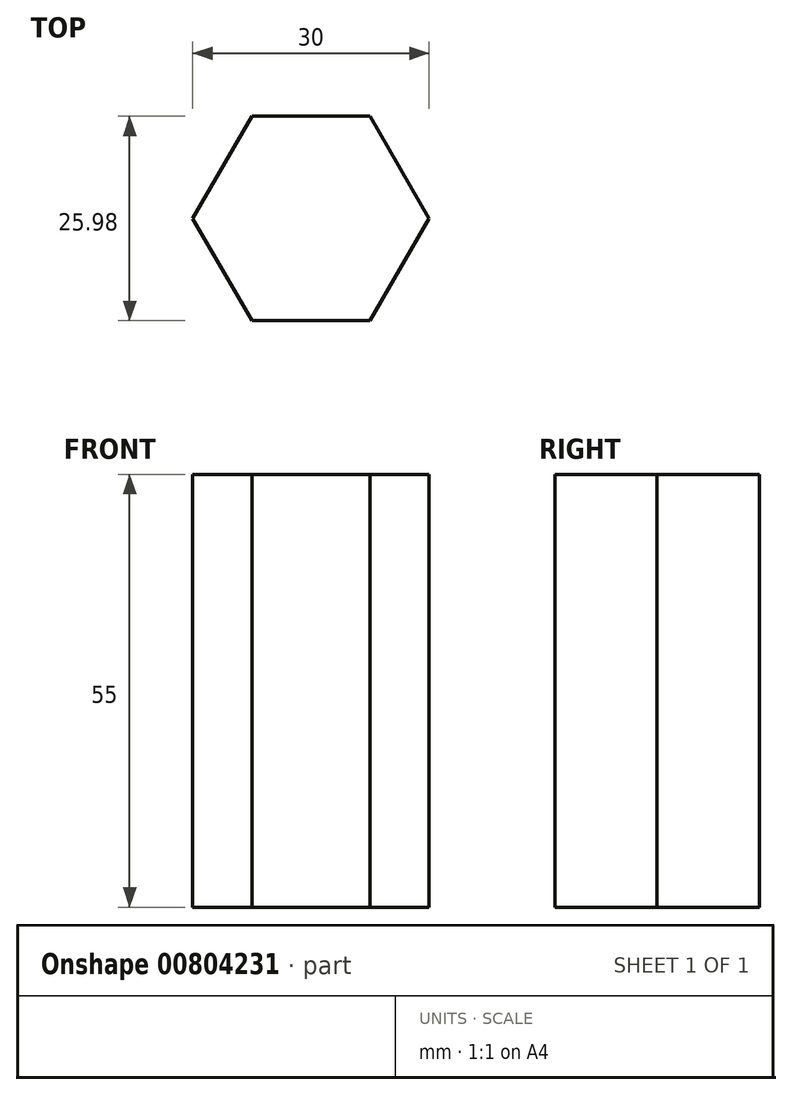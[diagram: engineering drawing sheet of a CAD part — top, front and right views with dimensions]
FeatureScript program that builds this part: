
annotation { "Feature Type Name" : "Feature", "Feature Type Description" : "" }
export const myFeature = defineFeature(function(context is Context, id is Id, definition is map)
    precondition{}
    {
        {
            var Q0;
            Q0=qCreatedBy(makeId("Top.planeOp"),FACE);
            var sketch = newSketch(context, id + "F0", { "sketchPlane" : qUnion([Q0])});
            skCircle(sketch, "E0.cCircle", {"center": v(0, 0) * mm, "radius": 15 * mm, "construction": true});
            skLineSegment(sketch, "E0.0", {"start": v(15, 0) * mm, "end": v(7.5, -13) * mm});
            skLineSegment(sketch, "E0.1", {"start": v(7.5, -13) * mm, "end": v(-7.5, -13) * mm});
            skLineSegment(sketch, "E0.2", {"start": v(-7.5, -13) * mm, "end": v(-15, 0) * mm});
            skLineSegment(sketch, "E0.3", {"start": v(-15, 0) * mm, "end": v(-7.5, 13) * mm});
            skLineSegment(sketch, "E0.4", {"start": v(-7.5, 13) * mm, "end": v(7.5, 13) * mm});
            skLineSegment(sketch, "E0.5", {"start": v(7.5, 13) * mm, "end": v(15, 0) * mm});
            skSolve(sketch);
        }
        {
            var Q0;
            Q0 = qSketchRegion(id + "F0", true);
            extrude(context, id + "F1", {"entities" : qUnion([Q0]), "depth" : 55 * mm, "offsetDistance" : 25 * mm});
        }
    });
